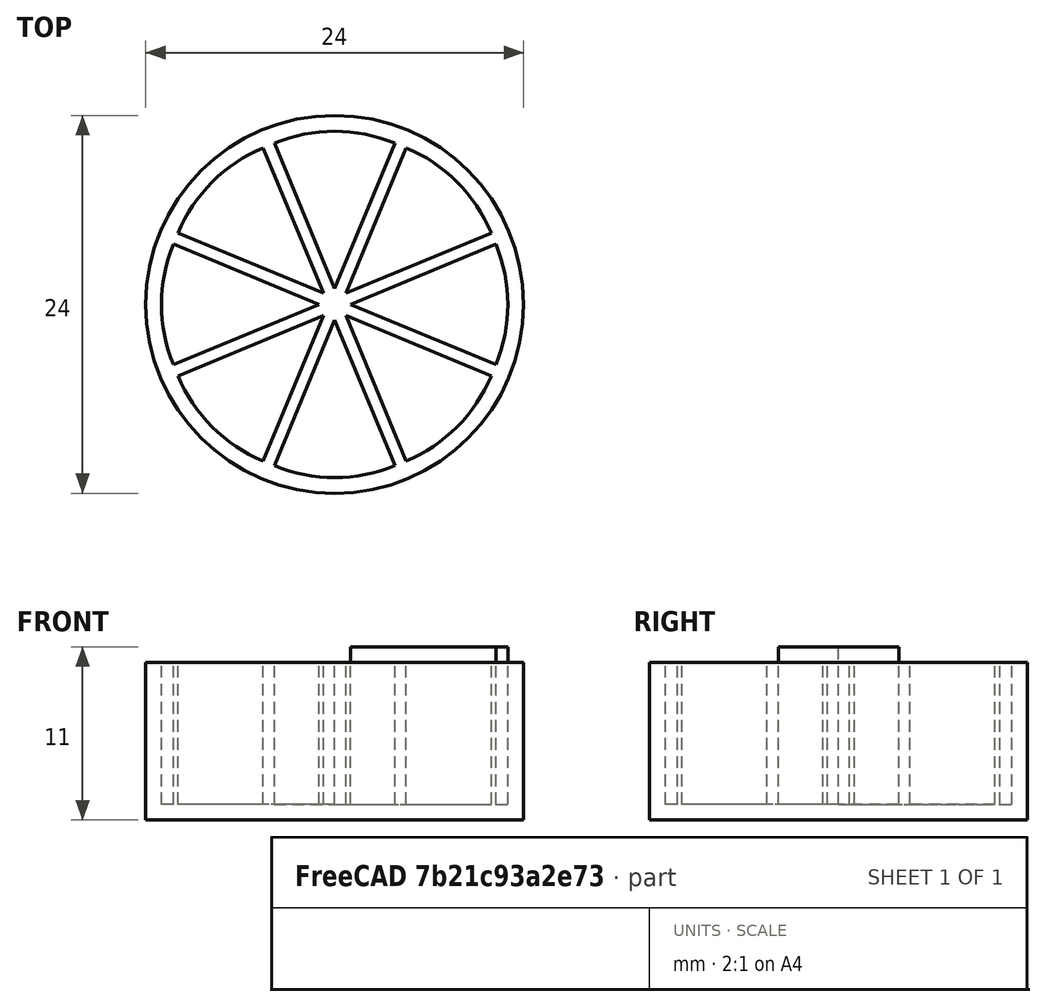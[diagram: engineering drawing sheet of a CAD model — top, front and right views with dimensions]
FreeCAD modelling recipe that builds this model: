
FCSTD DOCUMENT  (FreeCAD 0.18.4R)
Label: tutorial_freecad_ex11_c
License: All rights reserved
LicenseURL: http://en.wikipedia.org/wiki/All_rights_reserved
objects: Part::Cylinder×3, Part::FeaturePython×1, Part::Cut×1
note: 5 computed .brp shape members not serialized (recipe doc carries the construction recipe); baked Part::Feature solids carry a one-line shape summary decoded from their .brp

FEATURE [Part::Cylinder] Cylinder  label="base"
  Angle = 360
  AttacherType = Attacher::AttachEngine3D
  Height = 10
  Radius = 12
FEATURE [Part::Cylinder] Cylinder001  label="master_quesito"
  Angle = 45
  AttacherType = Attacher::AttachEngine3D
  Height = 10
  Placement = pos=(1,0,1) rot=(0,0,1;-0.392699rad)
  Radius = 10
FEATURE [Part::FeaturePython] Array  label="quesitos"  # Draft array (typed FeaturePython)
  Angle = 360
  ArrayType = 1
  Axis = (0,0,1)
  Base = -> Cylinder001
  Center = (0,0,0)
  Fuse = false
  IntervalAxis = (0,0,0)
  IntervalX = (1,0,0)
  IntervalY = (0,1,0)
  IntervalZ = (0,0,1)
  NumberPolar = 8
  NumberX = 2
  NumberY = 2
  NumberZ = 1
FEATURE [Part::Cylinder] Cylinder002  label="quesito_rosa"
  Angle = 45
  AttacherType = Attacher::AttachEngine3D
  Height = 10
  Placement = pos=(1,0,1) rot=(0,0,-1;0.392699rad)
  Radius = 10
FEATURE [Part::Cut] Cut  label="ficha"
  Base = -> Cylinder
  Refine = true
  Tool = -> Array
